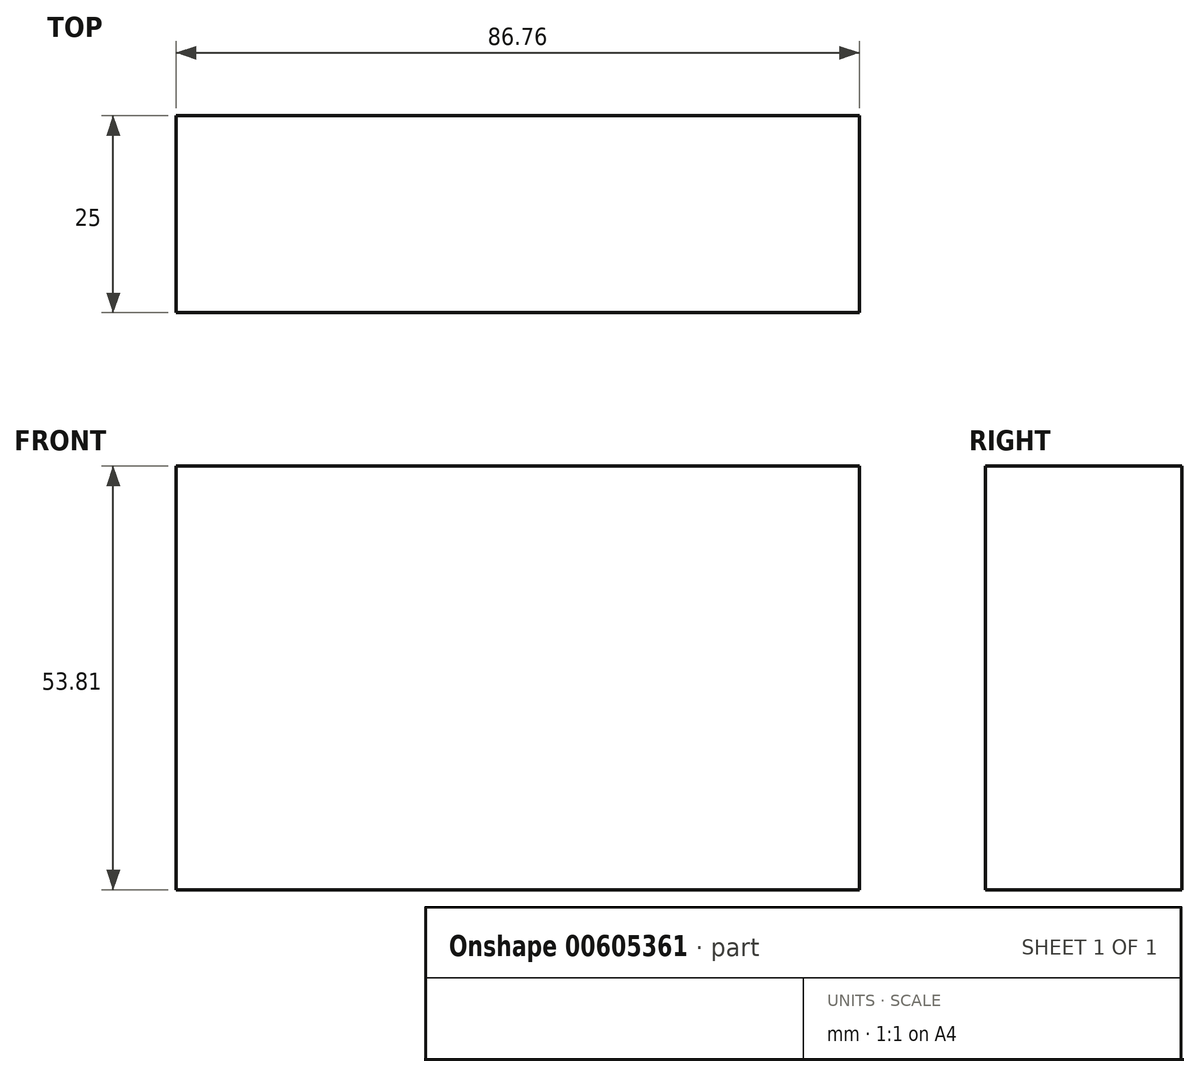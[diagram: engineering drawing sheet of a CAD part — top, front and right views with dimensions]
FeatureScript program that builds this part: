
annotation { "Feature Type Name" : "Feature", "Feature Type Description" : "" }
export const myFeature = defineFeature(function(context is Context, id is Id, definition is map)
    precondition{}
    {
        {
            var Q0;
            Q0=qCreatedBy(makeId("Front.planeOp"),FACE);
            var sketch = newSketch(context, id + "F0", { "sketchPlane" : qUnion([Q0])});
            skLineSegment(sketch, "E0.bottom", {"start": v(23.81, 26.44) * mm, "end": v(-62.95, 26.44) * mm});
            skLineSegment(sketch, "E0.top", {"start": v(23.81, -27.37) * mm, "end": v(-62.95, -27.37) * mm});
            skLineSegment(sketch, "E0.left", {"start": v(23.81, 26.44) * mm, "end": v(23.81, -27.37) * mm});
            skLineSegment(sketch, "E0.right", {"start": v(-62.95, 26.44) * mm, "end": v(-62.95, -27.37) * mm});
            skSolve(sketch);
        }
        {
            var Q0;
            Q0 = qSketchRegion(id + "F0", true);
            extrude(context, id + "F1", {"entities" : qUnion([Q0]), "depth" : 25 * mm, "offsetDistance" : 25 * mm});
        }
        {
            var Q0;
            Q0=makeQuery(id+"F1.opExtrude","SWEPT_FACE",FACE,{"disambiguationData":[OSD([sQuery(id+"F0.wireOp",EDGE,"E0.top")])]});
            var sketch = newSketch(context, id + "F2", { "sketchPlane" : qUnion([Q0])});
            skCircle(sketch, "E1", {"center": v(-50.6, 13.84) * mm, "radius": 4.97 * mm});
            skSolve(sketch);
        }
        {
            var Q0;
            Q0 = qSketchRegion(id + "F2", true);
            extrude(context, id + "F3", {"entities" : qUnion([Q0]), "operationType" : NewBodyOperationType.ADD, "oppositeDirection" : true, "depth" : 25 * mm, "offsetDistance" : 25 * mm});
        }
    });
